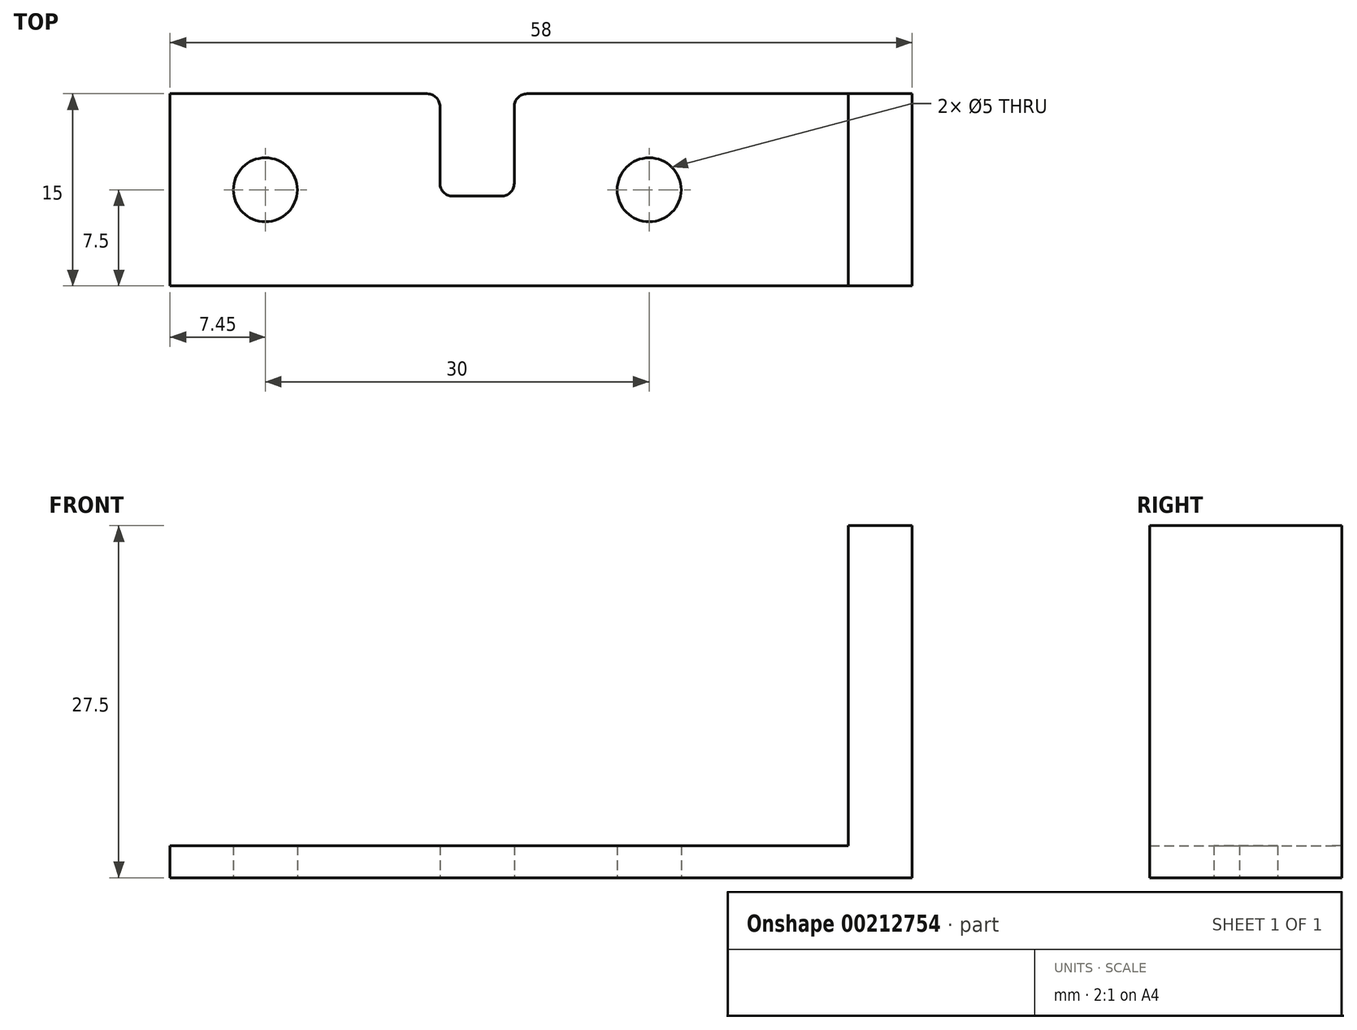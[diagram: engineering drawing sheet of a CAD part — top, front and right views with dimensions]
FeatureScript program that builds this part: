
annotation { "Feature Type Name" : "Feature", "Feature Type Description" : "" }
export const myFeature = defineFeature(function(context is Context, id is Id, definition is map)
    precondition{}
    {
        {
            var Q0;
            Q0=qCreatedBy(makeId("Top.planeOp"),FACE);
            var sketch = newSketch(context, id + "F0", { "sketchPlane" : qUnion([Q0])});
            skLineSegment(sketch, "E0", {"start": v(0, 0) * mm, "end": v(0, 15) * mm});
            skLineSegment(sketch, "E1", {"start": v(0, 15) * mm, "end": v(20.1, 15) * mm});
            skLineSegment(sketch, "E2", {"start": v(21.1, 14) * mm, "end": v(21.1, 8) * mm});
            skLineSegment(sketch, "E3", {"start": v(22.1, 7) * mm, "end": v(25.9, 7) * mm});
            skLineSegment(sketch, "E4", {"start": v(26.9, 8) * mm, "end": v(26.9, 14) * mm});
            skLineSegment(sketch, "E5", {"start": v(27.9, 15) * mm, "end": v(48, 15) * mm});
            skLineSegment(sketch, "E6", {"start": v(48, 15) * mm, "end": v(48, 0) * mm});
            skLineSegment(sketch, "E7", {"start": v(48, 0) * mm, "end": v(0, 0) * mm});
            skLineSegment(sketch, "E8", {"start": v(7.45, 15) * mm, "end": v(7.45, 0) * mm, "construction": true});
            skPoint(sketch, "E9", {"position": v(7.45, 7.5) * mm});
            skCircle(sketch, "E10", {"center": v(7.45, 7.5) * mm, "radius": 2.5 * mm});
            skLineSegment(sketch, "E11", {"start": v(37.45, 15) * mm, "end": v(37.45, 0) * mm, "construction": true});
            skPoint(sketch, "E12", {"position": v(37.45, 7.5) * mm});
            skCircle(sketch, "E13", {"center": v(37.45, 7.5) * mm, "radius": 2.5 * mm});
            skLineSegment(sketch, "E14", {"start": v(48, 7.5) * mm, "end": v(39.95, 7.5) * mm, "construction": true});
            skPoint(sketch, "E15.visualSharp", {"position": v(21.1, 7) * mm});
            skArc(sketch, "E15.filletArc", {"start": v(21.1, 8) * mm, "mid": v(21.4, 7.3) * mm, "end": v(22.1, 7) * mm});
            skPoint(sketch, "E16.visualSharp", {"position": v(26.9, 7) * mm});
            skArc(sketch, "E16.filletArc", {"start": v(25.9, 7) * mm, "mid": v(26.6, 7.3) * mm, "end": v(26.9, 8) * mm});
            skPoint(sketch, "E17.visualSharp", {"position": v(21.1, 15) * mm});
            skArc(sketch, "E17.filletArc", {"start": v(21.1, 14) * mm, "mid": v(20.8, 14.7) * mm, "end": v(20.1, 15) * mm});
            skPoint(sketch, "E18.visualSharp", {"position": v(26.9, 15) * mm});
            skArc(sketch, "E18.filletArc", {"start": v(27.9, 15) * mm, "mid": v(27.2, 14.7) * mm, "end": v(26.9, 14) * mm});
            skLineSegment(sketch, "E19", {"start": v(48, 15) * mm, "end": v(58, 15) * mm});
            skLineSegment(sketch, "E20", {"start": v(58, 15) * mm, "end": v(58, 0) * mm});
            skLineSegment(sketch, "E21", {"start": v(58, 0) * mm, "end": v(48, 0) * mm});
            skPoint(sketch, "E22", {"position": v(53, 15) * mm});
            skPoint(sketch, "E23", {"position": v(53, 0) * mm});
            skSolve(sketch);
        }
        {
            var Q0;
            Q0 = qSketchRegion(id + "F0", true);
            extrude(context, id + "F1", {"entities" : qUnion([Q0]), "depth" : 2.5 * mm});
        }
        {
            var Q0;
            Q0=qCreatedBy(makeId("Top.planeOp"),FACE);
            cPlane(context, id + "F2", {"entities" : qUnion([Q0]), "cplaneType" : CPlaneType.OFFSET, "offset" : 2.5 * mm, "width" : 150 * mm, "height" : 150 * mm});
        }
        {
            var Q0;
            Q0=qCreatedBy(id+"F2.planeOp",FACE);
            var sketch = newSketch(context, id + "F3", { "sketchPlane" : qUnion([Q0])});
            skPoint(sketch, "E24", {"position": v(48, 0) * mm});
            skLineSegment(sketch, "E25", {"start": v(0, 15) * mm, "end": v(0, 0) * mm, "construction": true});
            skLineSegment(sketch, "E26", {"start": v(0, 15) * mm, "end": v(58, 15) * mm, "construction": true});
            skLineSegment(sketch, "E27", {"start": v(58, 0) * mm, "end": v(58, 15) * mm});
            skLineSegment(sketch, "E28", {"start": v(58, 15) * mm, "end": v(48, 15) * mm});
            skPoint(sketch, "E29", {"position": v(53, 15) * mm});
            skLineSegment(sketch, "E30", {"start": v(53, 0) * mm, "end": v(53, 15) * mm});
            skLineSegment(sketch, "E31", {"start": v(48, 15) * mm, "end": v(58, 15) * mm});
            skLineSegment(sketch, "E32", {"start": v(0, 0) * mm, "end": v(48, 0) * mm, "construction": true});
            skLineSegment(sketch, "E33", {"start": v(53, 0) * mm, "end": v(58, 0) * mm});
            skLineSegment(sketch, "E34", {"start": v(58, 15) * mm, "end": v(53, 15) * mm});
            skLineSegment(sketch, "E35", {"start": v(53, 15) * mm, "end": v(53, 0) * mm});
            skLineSegment(sketch, "E36", {"start": v(48, 0) * mm, "end": v(53, 0) * mm});
            skSolve(sketch);
        }
        {
            var Q0;
            Q0 = qSketchRegion(id + "F3", true);
            extrude(context, id + "F4", {"entities" : qUnion([Q0]), "operationType" : NewBodyOperationType.ADD, "depth" : 25 * mm});
        }
    });
